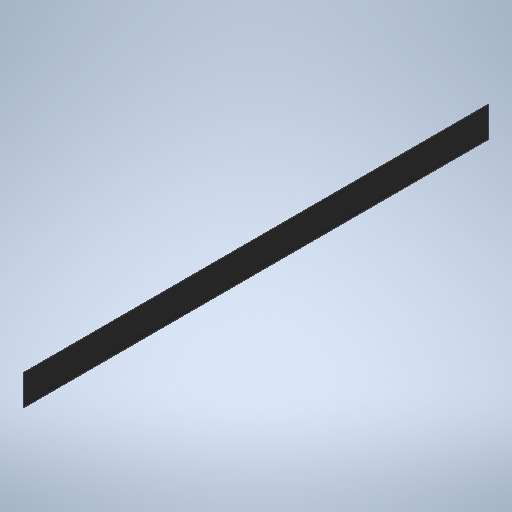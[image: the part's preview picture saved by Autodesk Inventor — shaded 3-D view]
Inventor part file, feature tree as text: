
AUTODESK INVENTOR PART (.ipt)
format: ipt  version: 2025.1 (Build 291241020, 241B)  size: 258,560 bytes
history: native  units: in
note: dims shown in document units (in); Inventor stores cm internally (conversion verified against a paired STEP export)
features: extrude x1, sketch x1
ambient origin geometry x8: Origin, YZ Plane, XZ Plane, XY Plane, X Axis, Y Axis, Z Axis, Center Point
bodies: Solid1 (feature_tree)
feature tree (2):
  extrude  "Extrusion1"  Depth=292.513in
  sketch  "Sketch1"  dims[d2=0.125in d3=0.0in d4=292.513in d5=19.157in]
